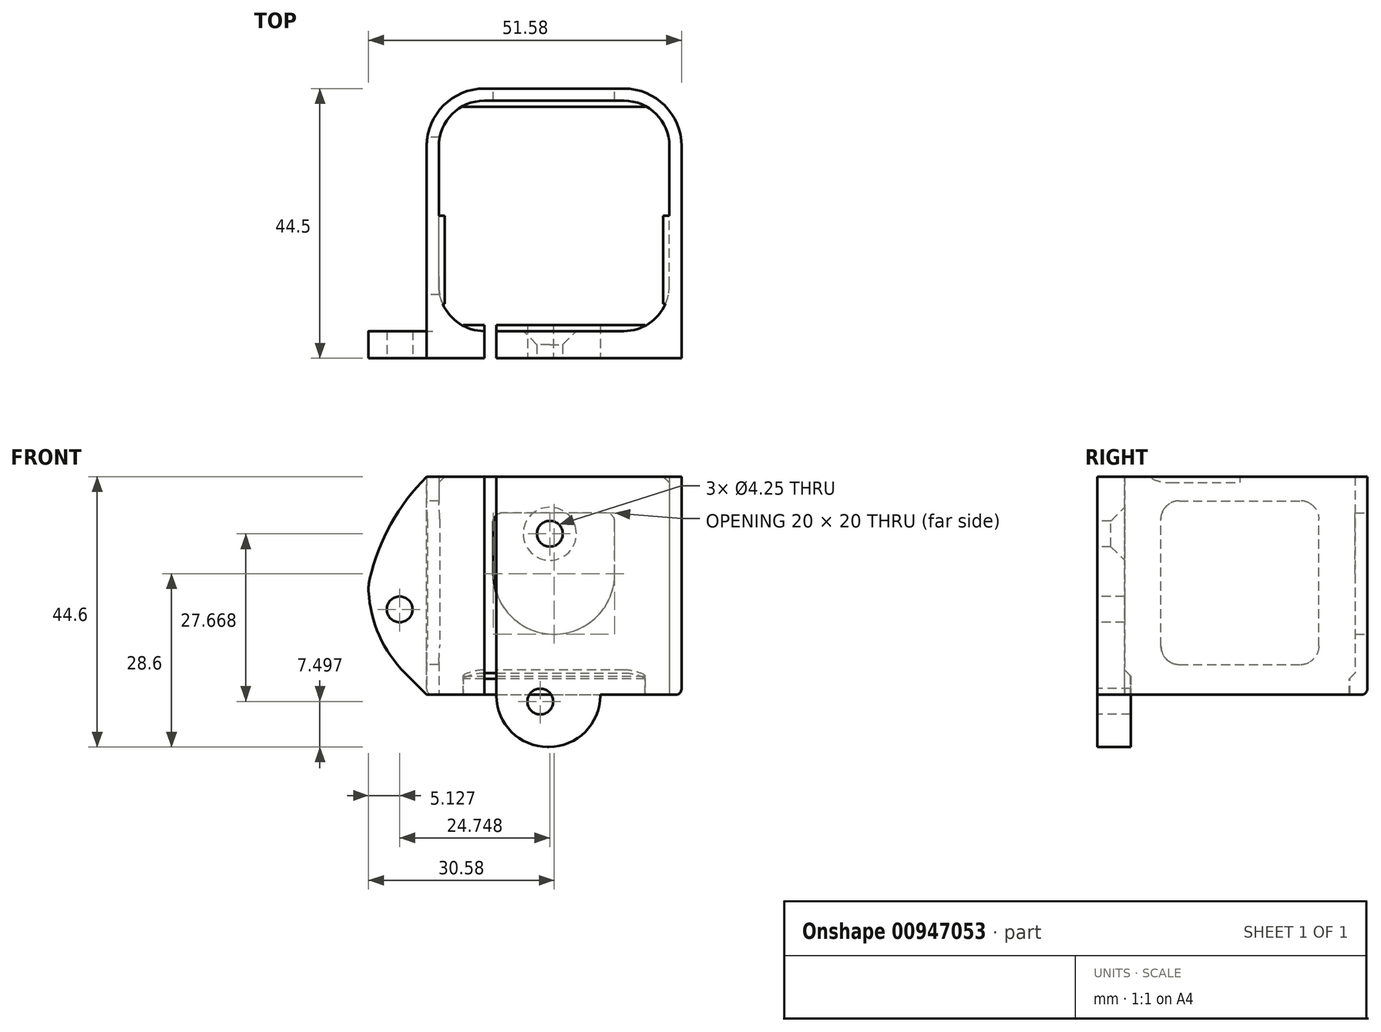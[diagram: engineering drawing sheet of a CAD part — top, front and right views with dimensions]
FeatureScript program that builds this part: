
annotation { "Feature Type Name" : "Feature", "Feature Type Description" : "" }
export const myFeature = defineFeature(function(context is Context, id is Id, definition is map)
    precondition{}
    {
        {
            var Q0;
            Q0=qCreatedBy(makeId("Top.planeOp"),FACE);
            var sketch = newSketch(context, id + "F0", { "sketchPlane" : qUnion([Q0])});
            skLineSegment(sketch, "E0.bottom", {"start": v(0, 0) * mm, "end": v(38, 0) * mm});
            skLineSegment(sketch, "E0.top", {"start": v(0, 38) * mm, "end": v(38, 38) * mm});
            skLineSegment(sketch, "E0.left", {"start": v(0, 0) * mm, "end": v(0, 38) * mm});
            skLineSegment(sketch, "E0.right", {"start": v(38, 0) * mm, "end": v(38, 38) * mm});
            skLineSegment(sketch, "E1", {"start": v(0, 0) * mm, "end": v(0, -2) * mm, "construction": true});
            skLineSegment(sketch, "E2", {"start": v(0, -2) * mm, "end": v(-2, -2) * mm, "construction": true});
            skLineSegment(sketch, "E3.bottom", {"start": v(-2, -2) * mm, "end": v(40, -2) * mm});
            skLineSegment(sketch, "E3.top", {"start": v(-2, 40) * mm, "end": v(40, 40) * mm});
            skLineSegment(sketch, "E3.left", {"start": v(-2, -2) * mm, "end": v(-2, 40) * mm});
            skLineSegment(sketch, "E3.right", {"start": v(40, -2) * mm, "end": v(40, 40) * mm});
            skSolve(sketch);
        }
        {
            var Q0;
            Q0=makeQuery(id+"F0.imprint","IMPRINT",FACE,{"disambiguationData":[TD([[makeQuery(id+"F0.imprint","IMPRINT",EDGE,{"derivedFrom":sQuery(id+"F0.wireOp",EDGE,"E0.bottom")}),-1.0]])]});
            extrude(context, id + "F1", {"entities" : qUnion([Q0]), "depth" : 36 * mm, "offsetDistance" : 25 * mm});
        }
        {
            var Q0;
            Q0=makeQuery(id+"F1.opExtrude","SWEPT_EDGE",EDGE,{"disambiguationData":[OSD([sQuery(id+"F0.wireOp",EDGE,"E0.bottom"),sQuery(id+"F0.wireOp",EDGE,"E0.left")])]});
            var Q1;
            Q1=makeQuery(id+"F1.opExtrude","SWEPT_EDGE",EDGE,{"disambiguationData":[OSD([sQuery(id+"F0.wireOp",EDGE,"E0.top"),sQuery(id+"F0.wireOp",EDGE,"E0.left")])]});
            var Q2;
            Q2=makeQuery(id+"F1.opExtrude","SWEPT_EDGE",EDGE,{"disambiguationData":[OSD([sQuery(id+"F0.wireOp",EDGE,"E0.top"),sQuery(id+"F0.wireOp",EDGE,"E0.right")])]});
            var Q3;
            Q3=makeQuery(id+"F1.opExtrude","SWEPT_EDGE",EDGE,{"disambiguationData":[OSD([sQuery(id+"F0.wireOp",EDGE,"E0.bottom"),sQuery(id+"F0.wireOp",EDGE,"E0.right")])]});
            fillet(context, id + "F2", {"entities" : qUnion([Q0, Q1, Q2, Q3]), "radius" : 7.5 * mm, "tangentPropagation" : true, "defaultsChanged" : true, "vertexSettings" : [], "allowEdgeOverflow" : false});
        }
        {
            var Q0;
            Q0=makeQuery(id+"F1.opExtrude","SWEPT_EDGE",EDGE,{"disambiguationData":[OSD([sQuery(id+"F0.wireOp",EDGE,"E3.top"),sQuery(id+"F0.wireOp",EDGE,"E3.right")])]});
            var Q1;
            Q1=makeQuery(id+"F1.opExtrude","SWEPT_EDGE",EDGE,{"disambiguationData":[OSD([sQuery(id+"F0.wireOp",EDGE,"E3.top"),sQuery(id+"F0.wireOp",EDGE,"E3.left")])]});
            fillet(context, id + "F3", {"entities" : qUnion([Q0, Q1]), "radius" : 9.5 * mm, "tangentPropagation" : true, "defaultsChanged" : false, "vertexSettings" : [], "allowEdgeOverflow" : false});
        }
        {
            var Q0;
            Q0=makeQuery(id+"F1.opExtrude","SWEPT_FACE",FACE,{"disambiguationData":[OSD([sQuery(id+"F0.wireOp",EDGE,"E0.top")])]});
            var sketch = newSketch(context, id + "F4", { "sketchPlane" : qUnion([Q0])});
            skLineSegment(sketch, "E4.bottom", {"start": v(4, 0) * mm, "end": v(34, 0) * mm});
            skLineSegment(sketch, "E4.top", {"start": v(4, 3.61) * mm, "end": v(34, 3.61) * mm});
            skLineSegment(sketch, "E4.left", {"start": v(4, 0) * mm, "end": v(4, 3.61) * mm});
            skLineSegment(sketch, "E4.right", {"start": v(34, 0) * mm, "end": v(34, 3.61) * mm});
            skSolve(sketch);
        }
        {
            var Q0;
            Q0=qSketchRegion(id+"F4",true);
            extrude(context, id + "F5", {"entities" : qUnion([Q0]), "operationType" : NewBodyOperationType.ADD, "depth" : 1 * mm, "offsetDistance" : 25 * mm});
        }
        {
            var Q0;
            Q0=makeQuery(id+"FW2NsXyDcc9ri8P_1.boolean.opBoolean","MERGE",FACE,{"derivedFrom":[makeQuery(id+"FSactm77qX1B1uA_1.boolean.opBoolean","MERGE",FACE,{"derivedFrom":[makeQuery(id+"F1.opExtrude","CAP_FACE",FACE,{"disambiguationData":[OSD([sQuery(id+"F0.wireOp",EDGE,"E0.bottom"),sQuery(id+"F0.wireOp",EDGE,"E0.top"),sQuery(id+"F0.wireOp",EDGE,"E0.left"),sQuery(id+"F0.wireOp",EDGE,"E0.right"),sQuery(id+"F0.wireOp",EDGE,"E3.bottom"),sQuery(id+"F0.wireOp",EDGE,"E3.top"),sQuery(id+"F0.wireOp",EDGE,"E3.left"),sQuery(id+"F0.wireOp",EDGE,"E3.right")])],"isStart":false}),makeQuery(id+"FSactm77qX1B1uA_1.opExtrude","SWEPT_FACE",FACE,{"disambiguationData":[OSD([sQuery(id+"FOY83ShXDJ28mBf_1.wireOp",EDGE,"vgOXgzTg-Qz0e-kkP7-poeQ-a0upuPTHjHjs.bottom")])]})]}),makeQuery(id+"FW2NsXyDcc9ri8P_1.opExtrude","SWEPT_FACE",FACE,{"disambiguationData":[OSD([sQuery(id+"FdfsZ7MiDT6VBPt_1.wireOp",EDGE,"T8VSNBQ1-C604-nsIn-AwT4-8OqMw17ya7MZ.top")])]}),makeQuery(id+"FW2NsXyDcc9ri8P_1.opExtrude","SWEPT_FACE",FACE,{"disambiguationData":[OSD([sQuery(id+"FdfsZ7MiDT6VBPt_1.wireOp",EDGE,"c4d735c6-f5d7-48ff-bfb1-ef2a3c96db213.MirrorCS")])]})]});
            var sketch = newSketch(context, id + "F6", { "sketchPlane" : qUnion([Q0])});
            skLineSegment(sketch, "E5.bottom", {"start": v(9.5, -2) * mm, "end": v(7.5, -2) * mm});
            skLineSegment(sketch, "E5.top", {"start": v(9.5, 2) * mm, "end": v(7.5, 2) * mm});
            skLineSegment(sketch, "E5.left", {"start": v(9.5, -2) * mm, "end": v(9.5, 2) * mm});
            skLineSegment(sketch, "E5.right", {"start": v(7.5, -2) * mm, "end": v(7.5, 2) * mm});
            skSolve(sketch);
        }
        {
            var Q0;
            Q0=makeQuery(id+"F1.opExtrude","SWEPT_FACE",FACE,{"disambiguationData":[OSD([sQuery(id+"F0.wireOp",EDGE,"E0.bottom")])]});
            var sketch = newSketch(context, id + "F7", { "sketchPlane" : qUnion([Q0])});
            skLineSegment(sketch, "E6.bottom", {"start": v(-34, 0) * mm, "end": v(-4, 0) * mm});
            skLineSegment(sketch, "E6.top", {"start": v(-34, 4.1) * mm, "end": v(-4, 4.1) * mm});
            skLineSegment(sketch, "E6.left", {"start": v(-34, 0) * mm, "end": v(-34, 4.1) * mm});
            skLineSegment(sketch, "E6.right", {"start": v(-4, 0) * mm, "end": v(-4, 4.1) * mm});
            skSolve(sketch);
        }
        {
            var Q0;
            Q0=qSketchRegion(id+"F7",true);
            extrude(context, id + "F8", {"entities" : qUnion([Q0]), "operationType" : NewBodyOperationType.ADD, "depth" : 1 * mm, "offsetDistance" : 25 * mm});
        }
        {
            var Q0;
            Q0=qSketchRegion(id+"F6",true);
            extrude(context, id + "F9", {"entities" : qUnion([Q0]), "operationType" : NewBodyOperationType.REMOVE, "oppositeDirection" : true, "depth" : 55.2 * mm, "offsetDistance" : 25 * mm});
        }
        {
            var Q0;
            Q0=makeQuery(id+"F1.opExtrude","CAP_EDGE",EDGE,{"disambiguationData":[OSD([sQuery(id+"F0.wireOp",EDGE,"E3.top")])],"isStart":true});
            fillet(context, id + "F10", {"entities" : qUnion([Q0]), "radius" : 1 * mm, "tangentPropagation" : true, "allowEdgeOverflow" : false});
        }
        {
            var Q0;
            Q0=makeQuery(id+"F1.opExtrude","SWEPT_FACE",FACE,{"disambiguationData":[OSD([sQuery(id+"F0.wireOp",EDGE,"E0.right")])]});
            var sketch = newSketch(context, id + "F11", { "sketchPlane" : qUnion([Q0])});
            skLineSegment(sketch, "E7.bottom", {"start": v(-4.5, 36) * mm, "end": v(-19, 36) * mm});
            skLineSegment(sketch, "E7.top", {"start": v(-4.5, 35) * mm, "end": v(-19, 35) * mm});
            skLineSegment(sketch, "E7.left", {"start": v(-4.5, 36) * mm, "end": v(-4.5, 35) * mm});
            skLineSegment(sketch, "E7.right", {"start": v(-19, 36) * mm, "end": v(-19, 35) * mm});
            skSolve(sketch);
        }
        {
            var Q0;
            Q0=qSketchRegion(id+"F11",true);
            extrude(context, id + "F12", {"entities" : qUnion([Q0]), "operationType" : NewBodyOperationType.ADD, "depth" : 1 * mm, "offsetDistance" : 25 * mm});
        }
        {
            var Q0;
            Q0=makeQuery(id+"F1.opExtrude","SWEPT_FACE",FACE,{"disambiguationData":[OSD([sQuery(id+"F0.wireOp",EDGE,"E0.left")])]});
            var sketch = newSketch(context, id + "F13", { "sketchPlane" : qUnion([Q0])});
            skLineSegment(sketch, "E8.bottom", {"start": v(4.5, 36) * mm, "end": v(19, 36) * mm});
            skLineSegment(sketch, "E8.top", {"start": v(4.5, 35) * mm, "end": v(19, 35) * mm});
            skLineSegment(sketch, "E8.left", {"start": v(4.5, 36) * mm, "end": v(4.5, 35) * mm});
            skLineSegment(sketch, "E8.right", {"start": v(19, 36) * mm, "end": v(19, 35) * mm});
            skSolve(sketch);
        }
        {
            var Q0;
            Q0=qSketchRegion(id+"F13",true);
            extrude(context, id + "F14", {"entities" : qUnion([Q0]), "operationType" : NewBodyOperationType.ADD, "depth" : 1 * mm, "offsetDistance" : 25 * mm});
        }
        {
            var Q0;
            Q0=makeQuery(id+"F14.opExtrude","CAP_EDGE",EDGE,{"disambiguationData":[OSD([sQuery(id+"F13.wireOp",EDGE,"E8.top")])],"isStart":false});
            var Q1;
            Q1=makeQuery(id+"F12.opExtrude","CAP_EDGE",EDGE,{"disambiguationData":[OSD([sQuery(id+"F11.wireOp",EDGE,"E7.top")])],"isStart":false});
            chamfer(context, id + "F15", {"entities" : qUnion([Q0, Q1]), "width" : 1 * mm, "tangentPropagation" : true});
        }
        {
            var Q0;
            {var subQ0=sQuery(id+"F7.wireOp",EDGE,"E6.left");var subQ1=sQuery(id+"F7.wireOp",EDGE,"E6.top");Q0=makeQuery(id+"F9.boolean.opBoolean","SPLIT",EDGE,{"disambiguationData":[TD([makeQuery(id+"F8.opExtrude","SWEPT_FACE",FACE,{"disambiguationData":[OSD([subQ0])]})])],"derivedFrom":makeQuery(id+"F8.opExtrude","CAP_EDGE",EDGE,{"disambiguationData":[OSD([subQ1])],"isStart":false})});}
            var Q1;
            {var subQ0=sQuery(id+"F7.wireOp",EDGE,"E6.right");var subQ1=sQuery(id+"F7.wireOp",EDGE,"E6.top");Q1=makeQuery(id+"F9.boolean.opBoolean","SPLIT",EDGE,{"disambiguationData":[TD([makeQuery(id+"F8.opExtrude","SWEPT_FACE",FACE,{"disambiguationData":[OSD([subQ0])]})])],"derivedFrom":makeQuery(id+"F8.opExtrude","CAP_EDGE",EDGE,{"disambiguationData":[OSD([subQ1])],"isStart":false})});}
            var Q2;
            Q2=makeQuery(id+"F5.opExtrude","CAP_EDGE",EDGE,{"disambiguationData":[OSD([sQuery(id+"F4.wireOp",EDGE,"E4.top")])],"isStart":false});
            chamfer(context, id + "F16", {"entities" : qUnion([Q0, Q1, Q2]), "width" : 1 * mm, "tangentPropagation" : true});
        }
        {
            var Q0;
            Q0=makeQuery(id+"F1.opExtrude","SWEPT_FACE",FACE,{"disambiguationData":[OSD([sQuery(id+"F0.wireOp",EDGE,"E3.left")])]});
            var sketch = newSketch(context, id + "F17", { "sketchPlane" : qUnion([Q0])});
            skLineSegment(sketch, "E9", {"start": v(-4, 1) * mm, "end": v(-4, 5) * mm});
            skLineSegment(sketch, "E10", {"start": v(-4, 5) * mm, "end": v(-6, 5) * mm});
            skLineSegment(sketch, "E11.bottom", {"start": v(-6, 5) * mm, "end": v(-32, 5) * mm});
            skLineSegment(sketch, "E11.top", {"start": v(-6, 32) * mm, "end": v(-32, 32) * mm});
            skLineSegment(sketch, "E11.left", {"start": v(-6, 5) * mm, "end": v(-6, 32) * mm});
            skLineSegment(sketch, "E11.right", {"start": v(-32, 5) * mm, "end": v(-32, 32) * mm});
            skSolve(sketch);
        }
        {
            var Q0;
            Q0=qSketchRegion(id+"F17",true);
            extrude(context, id + "F18", {"entities" : qUnion([Q0]), "operationType" : NewBodyOperationType.REMOVE, "oppositeDirection" : true, "depth" : 4.5 * mm, "offsetDistance" : 25 * mm});
        }
        {
            var Q0;
            Q0=makeQuery(id+"F18.boolean.opBoolean","COPY",EDGE,{"derivedFrom":makeQuery(id+"F18.opExtrude","SWEPT_EDGE",EDGE,{"disambiguationData":[OSD([sQuery(id+"F17.wireOp",EDGE,"E11.top"),sQuery(id+"F17.wireOp",EDGE,"E11.right")])]})});
            var Q1;
            Q1=makeQuery(id+"F18.boolean.opBoolean","COPY",EDGE,{"derivedFrom":makeQuery(id+"F18.opExtrude","SWEPT_EDGE",EDGE,{"disambiguationData":[OSD([sQuery(id+"F17.wireOp",EDGE,"E11.bottom"),sQuery(id+"F17.wireOp",EDGE,"E11.right")])]})});
            var Q2;
            Q2=makeQuery(id+"F18.boolean.opBoolean","COPY",EDGE,{"derivedFrom":makeQuery(id+"F18.opExtrude","SWEPT_EDGE",EDGE,{"disambiguationData":[OSD([sQuery(id+"F17.wireOp",EDGE,"E11.bottom"),sQuery(id+"F17.wireOp",EDGE,"E11.left")])]})});
            var Q3;
            Q3=makeQuery(id+"F18.boolean.opBoolean","COPY",EDGE,{"derivedFrom":makeQuery(id+"F18.opExtrude","SWEPT_EDGE",EDGE,{"disambiguationData":[OSD([sQuery(id+"F17.wireOp",EDGE,"E11.top"),sQuery(id+"F17.wireOp",EDGE,"E11.left")])]})});
            fillet(context, id + "F19", {"entities" : qUnion([Q0, Q1, Q2, Q3]), "radius" : 3 * mm, "tangentPropagation" : true, "allowEdgeOverflow" : false});
        }
        {
            var Q0;
            Q0=makeQuery(id+"F1.opExtrude","SWEPT_FACE",FACE,{"disambiguationData":[OSD([sQuery(id+"F0.wireOp",EDGE,"E3.top")])]});
            var sketch = newSketch(context, id + "F20", { "sketchPlane" : qUnion([Q0])});
            skLineSegment(sketch, "E12", {"start": v(-19, 1) * mm, "end": v(-19, 10) * mm});
            skLineSegment(sketch, "E13.bottom", {"start": v(-19, 10) * mm, "end": v(-29, 10) * mm});
            skLineSegment(sketch, "E13.top", {"start": v(-19, 30) * mm, "end": v(-29, 30) * mm});
            skLineSegment(sketch, "E13.left", {"start": v(-19, 10) * mm, "end": v(-19, 30) * mm, "construction": true});
            skLineSegment(sketch, "E13.right", {"start": v(-29, 10) * mm, "end": v(-29, 30) * mm});
            skLineSegment(sketch, "E14.MirrorCS", {"start": v(-19, 10) * mm, "end": v(-9, 10) * mm});
            skLineSegment(sketch, "E15.MirrorCS", {"start": v(-9, 10) * mm, "end": v(-9, 30) * mm});
            skLineSegment(sketch, "E16.MirrorCS", {"start": v(-19, 30) * mm, "end": v(-9, 30) * mm});
            skSolve(sketch);
        }
        {
            var Q0;
            Q0=makeQuery(id+"F20.imprint","IMPRINT",FACE,{"disambiguationData":[TD([[makeQuery(id+"F20.imprint","IMPRINT",EDGE,{"derivedFrom":sQuery(id+"F20.wireOp",EDGE,"E13.bottom")}),-1.0]])]});
            var Q1;
            Q1=sQuery(id+"F20.wireOp",EDGE,"E13.left");
            var Q2;
            Q2=sQuery(id+"F20.wireOp",EDGE,"E13.bottom");
            var Q3;
            Q3=sQuery(id+"F20.wireOp",EDGE,"E14.MirrorCS");
            var Q4;
            Q4=sQuery(id+"F20.wireOp",EDGE,"E15.MirrorCS");
            var Q5;
            Q5=sQuery(id+"F20.wireOp",EDGE,"E16.MirrorCS");
            var Q6;
            Q6=sQuery(id+"F20.wireOp",EDGE,"E13.top");
            var Q7;
            Q7=sQuery(id+"F20.wireOp",EDGE,"E13.right");
            extrude(context, id + "F21", {"entities" : qUnion([Q0]), "operationType" : NewBodyOperationType.REMOVE, "surfaceEntities" : qUnion([Q1, Q2, Q3, Q4, Q5, Q6, Q7]), "oppositeDirection" : true, "depth" : 5.1 * mm, "offsetDistance" : 25 * mm});
        }
        {
            var Q0;
            Q0=makeQuery(id+"F21.boolean.opBoolean","COPY",EDGE,{"derivedFrom":makeQuery(id+"F21.opExtrude","SWEPT_EDGE",EDGE,{"disambiguationData":[OSD([sQuery(id+"F20.wireOp",EDGE,"E14.MirrorCS"),sQuery(id+"F20.wireOp",EDGE,"E15.MirrorCS")])]})});
            var Q1;
            Q1=makeQuery(id+"F21.boolean.opBoolean","COPY",EDGE,{"derivedFrom":makeQuery(id+"F21.opExtrude","SWEPT_EDGE",EDGE,{"disambiguationData":[OSD([sQuery(id+"F20.wireOp",EDGE,"E13.bottom"),sQuery(id+"F20.wireOp",EDGE,"E13.right")])]})});
            fillet(context, id + "F22", {"entities" : qUnion([Q0, Q1]), "radius" : 10 * mm, "tangentPropagation" : true, "allowEdgeOverflow" : false});
        }
        {
            var Q0;
            Q0=makeQuery(id+"F21.boolean.opBoolean","COPY",EDGE,{"derivedFrom":makeQuery(id+"F21.opExtrude","SWEPT_EDGE",EDGE,{"disambiguationData":[OSD([sQuery(id+"F20.wireOp",EDGE,"E13.top"),sQuery(id+"F20.wireOp",EDGE,"E13.right")])]})});
            var Q1;
            Q1=makeQuery(id+"F21.boolean.opBoolean","COPY",EDGE,{"derivedFrom":makeQuery(id+"F21.opExtrude","SWEPT_EDGE",EDGE,{"disambiguationData":[OSD([sQuery(id+"F20.wireOp",EDGE,"E15.MirrorCS"),sQuery(id+"F20.wireOp",EDGE,"E16.MirrorCS")])]})});
            fillet(context, id + "F23", {"entities" : qUnion([Q0, Q1]), "radius" : 1.5 * mm, "tangentPropagation" : true, "allowEdgeOverflow" : false});
        }
        {
            var Q0;
            Q0=qCreatedBy(makeId("Front.planeOp"),FACE);
            cPlane(context, id + "F24", {"entities" : qUnion([Q0]), "cplaneType" : CPlaneType.OFFSET, "offset" : 4.5 * mm, "width" : 150 * mm, "height" : 150 * mm});
        }
        {
            var Q0;
            Q0=qCreatedBy(id+"F24.planeOp",FACE);
            var sketch = newSketch(context, id + "F25", { "sketchPlane" : qUnion([Q0])});
            skCircle(sketch, "E17", {"center": v(9.52, 13.19) * mm, "radius": 16 * mm, "construction": true});
            skCircle(sketch, "E18", {"center": v(18.3, 26.57) * mm, "radius": 2.12 * mm});
            skCircle(sketch, "E19.1.0", {"center": v(-6.45, 14.1) * mm, "radius": 2.12 * mm});
            skCircle(sketch, "E19.2.0", {"center": v(16.72, -1.1) * mm, "radius": 2.12 * mm});
            skPoint(sketch, "E19.center", {"position": v(22.8, 19.14) * mm});
            skSolve(sketch);
        }
        {
            var Q0;
            {var subQ0=sQuery(id+"F0.wireOp",EDGE,"E3.right");var subQ3=sQuery(id+"F0.wireOp",EDGE,"E3.bottom");Q0=makeQuery(id+"F9.boolean.opBoolean","SPLIT",FACE,{"disambiguationData":[TD([makeQuery(id+"F1.opExtrude","SWEPT_FACE",FACE,{"disambiguationData":[OSD([subQ0])]})])],"derivedFrom":makeQuery(id+"F1.opExtrude","SWEPT_FACE",FACE,{"disambiguationData":[OSD([subQ3])]})});}
            extrude(context, id + "F26", {"entities" : qUnion([Q0]), "operationType" : NewBodyOperationType.ADD, "depth" : 2.5 * mm, "offsetDistance" : 25 * mm});
        }
        {
            var Q0;
            {var subQ0=makeQuery(id+"F5.opExtrude","SWEPT_FACE",FACE,{"disambiguationData":[OSD([sQuery(id+"F4.wireOp",EDGE,"E4.bottom")])]});var subQ1=sQuery(id+"F0.wireOp",EDGE,"E3.right");var subQ2=sQuery(id+"F0.wireOp",EDGE,"E3.bottom");var subQ3=makeQuery(id+"F1.opExtrude","CAP_FACE",FACE,{"disambiguationData":[OSD([sQuery(id+"F0.wireOp",EDGE,"E0.bottom"),sQuery(id+"F0.wireOp",EDGE,"E0.top"),sQuery(id+"F0.wireOp",EDGE,"E0.left"),sQuery(id+"F0.wireOp",EDGE,"E0.right"),subQ2,sQuery(id+"F0.wireOp",EDGE,"E3.top"),sQuery(id+"F0.wireOp",EDGE,"E3.left"),subQ1])],"isStart":true});var subQ4=makeQuery(id+"F8.opExtrude","SWEPT_FACE",FACE,{"disambiguationData":[OSD([sQuery(id+"F7.wireOp",EDGE,"E6.bottom")])]});Q0=makeQuery(id+"F26.boolean.opBoolean","MERGE",FACE,{"derivedFrom":[makeQuery(id+"F8.boolean.opBoolean","MERGE",FACE,{"derivedFrom":[makeQuery(id+"F5.boolean.opBoolean","MERGE",FACE,{"derivedFrom":[subQ3,subQ0]}),subQ4]}),makeQuery(id+"F26.opExtrude","SWEPT_FACE",FACE,{"disambiguationData":[OSD([subQ2]),TDD([makeQuery(id+"F9.boolean.opBoolean","SPLIT",EDGE,{"disambiguationData":[TD([makeQuery(id+"F1.opExtrude","SWEPT_FACE",FACE,{"disambiguationData":[OSD([subQ1])]})])],"derivedFrom":makeQuery(id+"F1.opExtrude","CAP_EDGE",EDGE,{"disambiguationData":[OSD([subQ2])],"isStart":true})})])]})]});}
            var sketch = newSketch(context, id + "F27", { "sketchPlane" : qUnion([Q0])});
            skLineSegment(sketch, "E20", {"start": v(26.6, -1) * mm, "end": v(26.6, 4.5) * mm});
            skSolve(sketch);
        }
        {
            var Q0;
            {var subQ0=sQuery(id+"F0.wireOp",EDGE,"E3.left");var subQ3=sQuery(id+"F0.wireOp",EDGE,"E3.bottom");Q0=makeQuery(id+"F9.boolean.opBoolean","SPLIT",FACE,{"disambiguationData":[TD([makeQuery(id+"F1.opExtrude","SWEPT_FACE",FACE,{"disambiguationData":[OSD([subQ0])]})])],"derivedFrom":makeQuery(id+"F1.opExtrude","SWEPT_FACE",FACE,{"disambiguationData":[OSD([subQ3])]})});}
            extrude(context, id + "F28", {"entities" : qUnion([Q0]), "operationType" : NewBodyOperationType.ADD, "depth" : 2.5 * mm, "offsetDistance" : 25 * mm});
        }
        {
            var Q0;
            {var subQ0=sQuery(id+"F0.wireOp",EDGE,"E3.left");var subQ1=sQuery(id+"F0.wireOp",EDGE,"E3.bottom");Q0=makeQuery(id+"F28.boolean.opBoolean","MERGE",FACE,{"derivedFrom":[makeQuery(id+"F1.opExtrude","SWEPT_FACE",FACE,{"disambiguationData":[OSD([subQ0])]}),makeQuery(id+"F28.opExtrude","SWEPT_FACE",FACE,{"disambiguationData":[OSD([subQ1,subQ0]),TDD([makeQuery(id+"F1.opExtrude","SWEPT_EDGE",EDGE,{"disambiguationData":[OSD([subQ1,subQ0])]})])]})]});}
            var sketch = newSketch(context, id + "F29", { "sketchPlane" : qUnion([Q0])});
            skLineSegment(sketch, "E21.0", {"start": v(4.5, 36) * mm, "end": v(4.5, 1) * mm});
            skLineSegment(sketch, "E22.0", {"start": v(0, 4.1) * mm, "end": v(0, 36) * mm});
            skLineSegment(sketch, "E23.0", {"start": v(4.5, 1) * mm, "end": v(4.5, 0) * mm});
            skLineSegment(sketch, "E24.0", {"start": v(4.5, 0) * mm, "end": v(-30.5, 0) * mm});
            skLineSegment(sketch, "E25", {"start": v(0, 4.1) * mm, "end": v(0, 0) * mm});
            skLineSegment(sketch, "E26", {"start": v(0, 0) * mm, "end": v(4.5, 0) * mm});
            skSolve(sketch);
        }
        {
            var Q0;
            {var subQ15=sQuery(id+"F29.wireOp",EDGE,"E21.0");Q0=makeQuery(id+"F29.imprint","IMPRINT",FACE,{"disambiguationData":[TD([[makeQuery(id+"F29.imprint","IMPRINT",EDGE,{"derivedFrom":subQ15}),-1.0]])]});}
            var Q1;
            {var subQ0=sQuery(id+"F29.wireOp",EDGE,"E23.0");Q1=makeQuery(id+"F29.imprint","IMPRINT",FACE,{"disambiguationData":[TD([[makeQuery(id+"F29.imprint","IMPRINT",EDGE,{"derivedFrom":subQ0}),-1.0]])]});}
            extrude(context, id + "F30", {"entities" : qUnion([Q0, Q1]), "operationType" : NewBodyOperationType.ADD, "depth" : 9.6 * mm, "offsetDistance" : 25 * mm});
        }
        {
            var Q0;
            {var subQ0=sQuery(id+"F27.wireOp",EDGE,"E20");Q0=makeQuery(id+"F27.imprint","IMPRINT",FACE,{"disambiguationData":[TD([[makeQuery(id+"F27.imprint","IMPRINT",EDGE,{"derivedFrom":subQ0}),1.0]])]});}
            extrude(context, id + "F31", {"entities" : qUnion([Q0]), "operationType" : NewBodyOperationType.ADD, "depth" : 8.6 * mm, "offsetDistance" : 25 * mm});
        }
        {
            var Q0;
            Q0 = qSketchRegion(id + "F25", true);
            extrude(context, id + "F32", {"entities" : qUnion([Q0]), "operationType" : NewBodyOperationType.REMOVE, "oppositeDirection" : true, "depth" : 25 * mm, "offsetDistance" : 25 * mm});
        }
        {
            var Q0;
            {var subQ1=sQuery(id+"F0.wireOp",EDGE,"E0.bottom");Q0=makeQuery(id+"F32.boolean.opBoolean","INTERSECT",EDGE,{"derivedFrom":[makeQuery(id+"F9.boolean.opBoolean","SPLIT",FACE,{"disambiguationData":[TD([makeQuery(id+"F9.opExtrude","SWEPT_FACE",FACE,{"disambiguationData":[OSD([sQuery(id+"F6.wireOp",EDGE,"E5.right")])]})])],"derivedFrom":makeQuery(id+"F1.opExtrude","SWEPT_FACE",FACE,{"disambiguationData":[OSD([subQ1])]})}),makeQuery(id+"F32.opExtrude","SWEPT_FACE",FACE,{"disambiguationData":[OSD([sQuery(id+"F25.wireOp",EDGE,"E18")])]})]});}
            var Q1;
            {var subQ0=sQuery(id+"FnWSPEZsh4SQCPz_1.wireOp",EDGE,"vNEy9e3T-qnrN-Ldcr-83SG-uP68q5c3sJvn");var subQ1=sQuery(id+"FnWSPEZsh4SQCPz_1.wireOp",EDGE,"416f8ad6-045a-4814-b1a7-002255f692be.0");Q1=makeQuery(id+"F32.boolean.opBoolean","INTERSECT",EDGE,{"derivedFrom":[makeQuery(id+"FL4Ru4QrY1cXg71_1.boolean.opBoolean","MERGE",FACE,{"derivedFrom":[makeQuery(id+"FPDlHmQ6RULO4E6_1.opExtrude","SWEPT_FACE",FACE,{"disambiguationData":[OSD([subQ1,subQ0])]}),makeQuery(id+"FL4Ru4QrY1cXg71_1.opExtrude","SWEPT_FACE",FACE,{"disambiguationData":[OSD([subQ1,subQ0])]})]}),makeQuery(id+"F32.opExtrude","SWEPT_FACE",FACE,{"disambiguationData":[OSD([sQuery(id+"F25.wireOp",EDGE,"E19.1.0")])]})]});}
            var Q2;
            {var subQ0=sQuery(id+"FnWSPEZsh4SQCPz_1.wireOp",EDGE,"vNEy9e3T-qnrN-Ldcr-83SG-uP68q5c3sJvn");var subQ1=sQuery(id+"FnWSPEZsh4SQCPz_1.wireOp",EDGE,"416f8ad6-045a-4814-b1a7-002255f692be.0");Q2=makeQuery(id+"F32.boolean.opBoolean","INTERSECT",EDGE,{"derivedFrom":[makeQuery(id+"FL4Ru4QrY1cXg71_1.boolean.opBoolean","MERGE",FACE,{"derivedFrom":[makeQuery(id+"FPDlHmQ6RULO4E6_1.opExtrude","SWEPT_FACE",FACE,{"disambiguationData":[OSD([subQ1,subQ0])]}),makeQuery(id+"FL4Ru4QrY1cXg71_1.opExtrude","SWEPT_FACE",FACE,{"disambiguationData":[OSD([subQ1,subQ0])]})]}),makeQuery(id+"F32.opExtrude","SWEPT_FACE",FACE,{"disambiguationData":[OSD([sQuery(id+"F25.wireOp",EDGE,"E19.2.0")])]})]});}
            chamfer(context, id + "F33", {"entities" : qUnion([Q0, Q1, Q2]), "width" : 2.25 * mm, "tangentPropagation" : true});
        }
        {
            var Q0;
            Q0=makeQuery(id+"F30.opExtrude","CAP_FACE",FACE,{"disambiguationData":[OSD([sQuery(id+"F0.wireOp",EDGE,"E3.bottom"),sQuery(id+"F0.wireOp",EDGE,"E3.left"),sQuery(id+"F29.wireOp",EDGE,"E21.0"),sQuery(id+"F29.wireOp",EDGE,"E22.0"),sQuery(id+"F29.wireOp",EDGE,"E23.0"),sQuery(id+"F29.wireOp",EDGE,"E24.0"),sQuery(id+"F29.wireOp",EDGE,"E25")])],"isStart":true});
            extrude(context, id + "F34", {"entities" : qUnion([Q0]), "operationType" : NewBodyOperationType.ADD, "endBound" : BoundingType.UP_TO_NEXT, "depth" : 25 * mm, "offsetDistance" : 25 * mm});
        }
        {
            var Q0;
            Q0=makeQuery(id+"F31.opExtrude","CAP_EDGE",EDGE,{"disambiguationData":[OSD([sQuery(id+"F27.wireOp",EDGE,"E20")])],"isStart":false});
            var Q1;
            Q1=makeQuery(id+"F31.opExtrude","CAP_EDGE",EDGE,{"disambiguationData":[OSD([sQuery(id+"F0.wireOp",EDGE,"E0.bottom"),sQuery(id+"F0.wireOp",EDGE,"E0.top"),sQuery(id+"F0.wireOp",EDGE,"E0.left"),sQuery(id+"F0.wireOp",EDGE,"E0.right"),sQuery(id+"F0.wireOp",EDGE,"E3.bottom"),sQuery(id+"F0.wireOp",EDGE,"E3.top"),sQuery(id+"F0.wireOp",EDGE,"E3.left"),sQuery(id+"F0.wireOp",EDGE,"E3.right"),sQuery(id+"F4.wireOp",EDGE,"E4.bottom"),sQuery(id+"F6.wireOp",EDGE,"E5.left"),sQuery(id+"F7.wireOp",EDGE,"E6.bottom")])],"isStart":false});
            fillet(context, id + "F35", {"entities" : qUnion([Q0, Q1]), "tangentPropagation" : true, "radius" : 8.45 * mm, "defaultsChanged" : true, "vertexSettings" : [], "allowEdgeOverflow" : false});
        }
        {
            var Q0;
            Q0=makeQuery(id+"F30.opExtrude","CAP_EDGE",EDGE,{"disambiguationData":[OSD([sQuery(id+"F29.wireOp",EDGE,"E24.0")])],"isStart":false});
            var Q1;
            Q1=makeQuery(id+"F30.opExtrude","CAP_EDGE",EDGE,{"disambiguationData":[OSD([sQuery(id+"F0.wireOp",EDGE,"E3.bottom"),sQuery(id+"F0.wireOp",EDGE,"E3.left")])],"isStart":false});
            chamfer(context, id + "F36", {"entities" : qUnion([Q0, Q1]), "width" : 9.6 * mm, "tangentPropagation" : true});
        }
        {
            var Q0;
            {var subQ0=sQuery(id+"F29.wireOp",EDGE,"E24.0");Q0=makeQuery(id+"F36.opChamfer","BLEND_EDGE",EDGE,{"blendedFrom":[makeQuery(id+"F30.opExtrude","CAP_EDGE",EDGE,{"disambiguationData":[OSD([subQ0])],"isStart":false}),makeQuery(id+"F30.opExtrude","CAP_FACE",FACE,{"disambiguationData":[OSD([sQuery(id+"F0.wireOp",EDGE,"E3.bottom"),sQuery(id+"F0.wireOp",EDGE,"E3.left"),sQuery(id+"F29.wireOp",EDGE,"E21.0"),sQuery(id+"F29.wireOp",EDGE,"E22.0"),sQuery(id+"F29.wireOp",EDGE,"E23.0"),subQ0,sQuery(id+"F29.wireOp",EDGE,"E25")])],"isStart":false})],"blendedInto":[makeQuery(id+"F30.opExtrude","CAP_FACE",FACE,{"disambiguationData":[OSD([sQuery(id+"F0.wireOp",EDGE,"E3.bottom"),sQuery(id+"F0.wireOp",EDGE,"E3.left"),sQuery(id+"F29.wireOp",EDGE,"E21.0"),sQuery(id+"F29.wireOp",EDGE,"E22.0"),sQuery(id+"F29.wireOp",EDGE,"E23.0"),subQ0,sQuery(id+"F29.wireOp",EDGE,"E25")])],"isStart":false})]});}
            fillet(context, id + "F37", {"entities" : qUnion([Q0]), "tangentPropagation" : true, "radius" : 20.63 * mm, "defaultsChanged" : false, "vertexSettings" : [], "allowEdgeOverflow" : false});
        }
        {
            var Q0;
            {var subQ0=sQuery(id+"F0.wireOp",EDGE,"E3.left");var subQ1=sQuery(id+"F0.wireOp",EDGE,"E3.bottom");Q0=makeQuery(id+"F36.opChamfer","BLEND_EDGE",EDGE,{"blendedFrom":[makeQuery(id+"F30.opExtrude","CAP_EDGE",EDGE,{"disambiguationData":[OSD([subQ1,subQ0])],"isStart":false}),makeQuery(id+"F30.opExtrude","CAP_FACE",FACE,{"disambiguationData":[OSD([subQ1,subQ0,sQuery(id+"F29.wireOp",EDGE,"E21.0"),sQuery(id+"F29.wireOp",EDGE,"E22.0"),sQuery(id+"F29.wireOp",EDGE,"E23.0"),sQuery(id+"F29.wireOp",EDGE,"E24.0"),sQuery(id+"F29.wireOp",EDGE,"E25")])],"isStart":false})],"blendedInto":[makeQuery(id+"F30.opExtrude","CAP_FACE",FACE,{"disambiguationData":[OSD([subQ1,subQ0,sQuery(id+"F29.wireOp",EDGE,"E21.0"),sQuery(id+"F29.wireOp",EDGE,"E22.0"),sQuery(id+"F29.wireOp",EDGE,"E23.0"),sQuery(id+"F29.wireOp",EDGE,"E24.0"),sQuery(id+"F29.wireOp",EDGE,"E25")])],"isStart":false})]});}
            fillet(context, id + "F38", {"entities" : qUnion([Q0]), "tangentPropagation" : true, "radius" : 35.2 * mm, "defaultsChanged" : true, "vertexSettings" : [], "allowEdgeOverflow" : false});
        }
        {
            var Q0;
            {var subQ0=sQuery(id+"F29.wireOp",EDGE,"E25");var subQ1=sQuery(id+"F29.wireOp",EDGE,"E24.0");var subQ2=sQuery(id+"F29.wireOp",EDGE,"E23.0");var subQ3=sQuery(id+"F29.wireOp",EDGE,"E22.0");var subQ4=sQuery(id+"F29.wireOp",EDGE,"E21.0");var subQ5=sQuery(id+"F0.wireOp",EDGE,"E3.left");var subQ6=sQuery(id+"F0.wireOp",EDGE,"E3.bottom");Q0=makeQuery(id+"F38.opFillet","BLEND_EDGE",EDGE,{"blendedFrom":[makeQuery(id+"F36.opChamfer","BLEND_EDGE",EDGE,{"blendedFrom":[makeQuery(id+"F30.opExtrude","CAP_EDGE",EDGE,{"disambiguationData":[OSD([subQ6,subQ5])],"isStart":false}),makeQuery(id+"F30.opExtrude","CAP_FACE",FACE,{"disambiguationData":[OSD([subQ6,subQ5,subQ4,subQ3,subQ2,subQ1,subQ0])],"isStart":false})],"blendedInto":[makeQuery(id+"F30.opExtrude","CAP_FACE",FACE,{"disambiguationData":[OSD([subQ6,subQ5,subQ4,subQ3,subQ2,subQ1,subQ0])],"isStart":false})]}),makeQuery(id+"F37.opFillet","BLEND_FACE",FACE,{"disambiguationData":[OSD([subQ6,subQ5,subQ4,subQ3,subQ2,subQ1,subQ0])]})],"blendedInto":[makeQuery(id+"F37.opFillet","BLEND_FACE",FACE,{"disambiguationData":[OSD([subQ6,subQ5,subQ4,subQ3,subQ2,subQ1,subQ0])]})]});}
            fillet(context, id + "F39", {"entities" : qUnion([Q0]), "tangentPropagation" : true, "radius" : 7 * mm, "defaultsChanged" : true, "vertexSettings" : [], "allowEdgeOverflow" : false});
        }
    });
